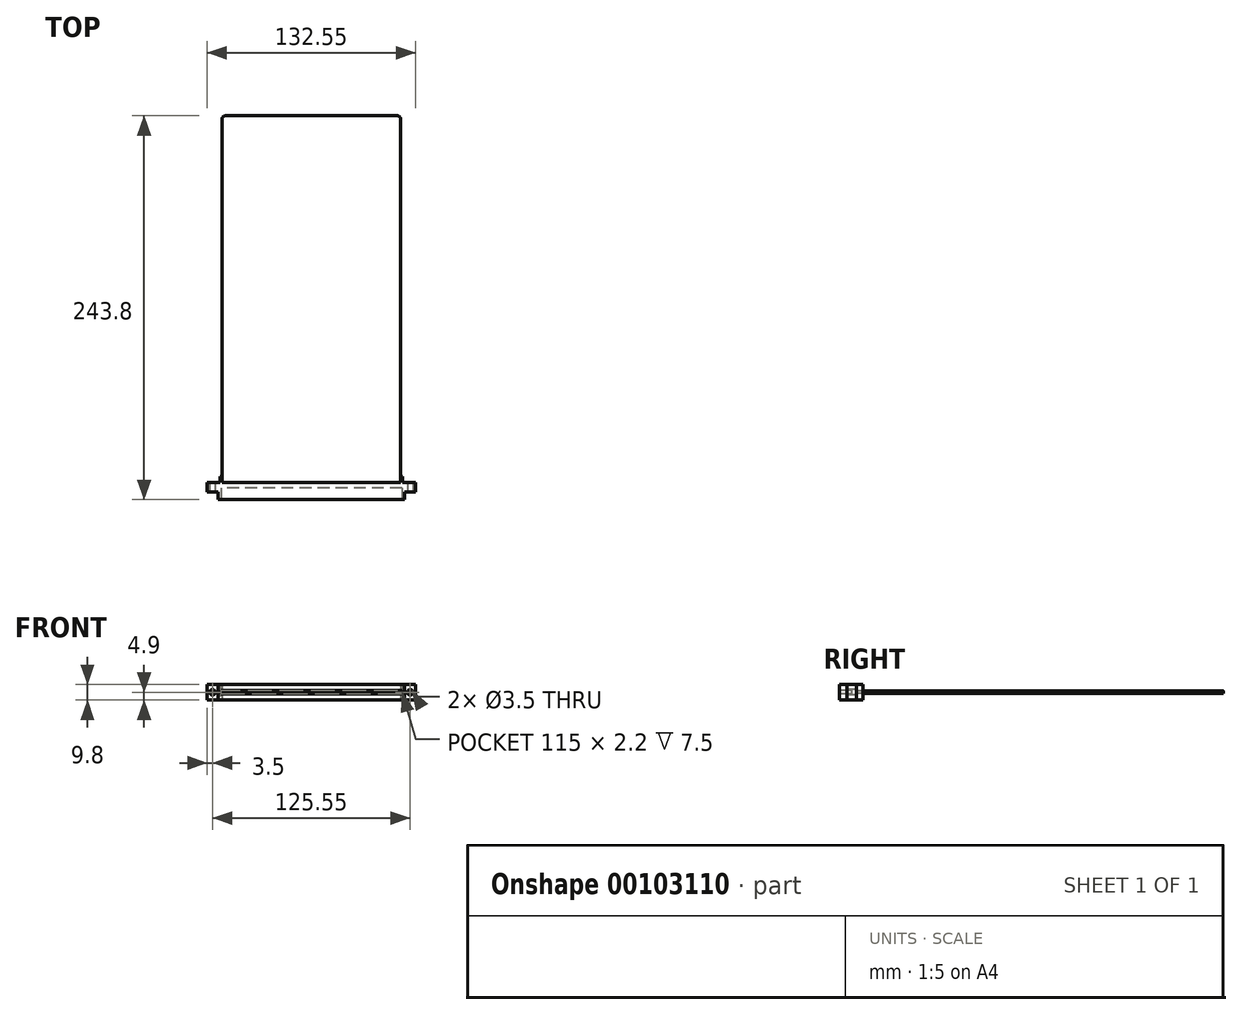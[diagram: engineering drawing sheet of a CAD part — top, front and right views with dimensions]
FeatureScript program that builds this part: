
annotation { "Feature Type Name" : "Feature", "Feature Type Description" : "" }
export const myFeature = defineFeature(function(context is Context, id is Id, definition is map)
    precondition{}
    {
        {
            var Q0;
            Q0=qCreatedBy(makeId("Top.planeOp"),FACE);
            var sketch = newSketch(context, id + "F0", { "sketchPlane" : qUnion([Q0])});
            skLineSegment(sketch, "E0.bottom", {"start": v(0, 6) * mm, "end": v(8.22, 6) * mm});
            skLineSegment(sketch, "E0.top", {"start": v(7, -4.8) * mm, "end": v(125.55, -4.8) * mm});
            skLineSegment(sketch, "E0.left", {"start": v(0, 6) * mm, "end": v(0, 0) * mm});
            skLineSegment(sketch, "E0.right", {"start": v(132.55, 6) * mm, "end": v(132.55, 0) * mm});
            skLineSegment(sketch, "E1.top", {"start": v(0, 0) * mm, "end": v(7, 0) * mm});
            skLineSegment(sketch, "E1.right", {"start": v(7, -4.8) * mm, "end": v(7, 0) * mm});
            skLineSegment(sketch, "E2.top", {"start": v(132.55, 0) * mm, "end": v(125.55, 0) * mm});
            skLineSegment(sketch, "E2.right", {"start": v(125.55, -4.8) * mm, "end": v(125.55, 0) * mm});
            skLineSegment(sketch, "E3.top", {"start": v(8.22, 10) * mm, "end": v(9.57, 10) * mm});
            skLineSegment(sketch, "E3.left", {"start": v(8.22, 6) * mm, "end": v(8.22, 10) * mm});
            skLineSegment(sketch, "E3.right", {"start": v(9.57, 6) * mm, "end": v(9.57, 10) * mm});
            skLineSegment(sketch, "E4.top", {"start": v(124.33, 10) * mm, "end": v(122.98, 10) * mm});
            skLineSegment(sketch, "E4.left", {"start": v(124.33, 6) * mm, "end": v(124.33, 10) * mm});
            skLineSegment(sketch, "E4.right", {"start": v(122.98, 6) * mm, "end": v(122.98, 10) * mm});
            skLineSegment(sketch, "E5.trimOffspring", {"start": v(124.33, 6) * mm, "end": v(132.55, 6) * mm});
            skLineSegment(sketch, "E6.trimOffspring", {"start": v(9.57, 6) * mm, "end": v(122.98, 6) * mm});
            skSolve(sketch);
        }
        {
            var Q0;
            Q0=makeQuery(id+"F0.imprint","IMPRINT",FACE,{"disambiguationData":[TD([[makeQuery(id+"F0.imprint","IMPRINT",EDGE,{"derivedFrom":sQuery(id+"F0.wireOp",EDGE,"E0.bottom")}),-1.0]])]});
            extrude(context, id + "F1", {"entities" : qUnion([Q0]), "depth" : 9.8 * mm});
        }
        {
            var Q0;
            Q0=makeQuery(id+"F1.opExtrude","SWEPT_FACE",FACE,{"disambiguationData":[OSD([sQuery(id+"F0.wireOp",EDGE,"E1.top")])]});
            var sketch = newSketch(context, id + "F2", { "sketchPlane" : qUnion([Q0])});
            skCircle(sketch, "E7", {"center": v(3.5, 4.9) * mm, "radius": 1.75 * mm});
            skPoint(sketch, "E7.centerSnap0", {"position": v(7, 4.9) * mm});
            skPoint(sketch, "E7.centerSnap1", {"position": v(3.5, 9.8) * mm});
            skSolve(sketch);
        }
        {
            var Q0;
            Q0=makeQuery(id+"F2.imprint","IMPRINT",FACE,{"disambiguationData":[TD([[makeQuery(id+"F2.imprint","IMPRINT",EDGE,{"derivedFrom":sQuery(id+"F2.wireOp",EDGE,"E7")}),1.0]])]});
            extrude(context, id + "F3", {"entities" : qUnion([Q0]), "operationType" : NewBodyOperationType.REMOVE, "oppositeDirection" : true, "depth" : 7 * mm});
        }
        {
            var Q0;
            Q0=makeQuery(id+"F1.opExtrude","SWEPT_FACE",FACE,{"disambiguationData":[OSD([sQuery(id+"F0.wireOp",EDGE,"E2.top")])]});
            var sketch = newSketch(context, id + "F4", { "sketchPlane" : qUnion([Q0])});
            skCircle(sketch, "E8", {"center": v(129.05, 4.9) * mm, "radius": 1.75 * mm});
            skPoint(sketch, "E8.centerSnap0", {"position": v(125.55, 4.9) * mm});
            skPoint(sketch, "E8.centerSnap1", {"position": v(129.05, 9.8) * mm});
            skSolve(sketch);
        }
        {
            var Q0;
            Q0 = qSketchRegion(id + "F4", true);
            var Q1;
            Q1=makeQuery(id+"F4.imprint","IMPRINT",FACE,{"disambiguationData":[TD([[makeQuery(id+"F4.imprint","IMPRINT",EDGE,{"derivedFrom":sQuery(id+"F4.wireOp",EDGE,"E8")}),1.0]])]});
            extrude(context, id + "F5", {"entities" : qUnion([Q0, Q1]), "operationType" : NewBodyOperationType.REMOVE, "oppositeDirection" : true, "depth" : 7 * mm});
        }
        {
            var Q0;
            Q0=makeQuery(id+"F1.opExtrude","SWEPT_FACE",FACE,{"disambiguationData":[OSD([sQuery(id+"F0.wireOp",EDGE,"E0.top")])]});
            var sketch = newSketch(context, id + "F6", { "sketchPlane" : qUnion([Q0])});
            skLineSegment(sketch, "E9.bottom", {"start": v(123.78, 6) * mm, "end": v(8.78, 6) * mm});
            skLineSegment(sketch, "E9.top", {"start": v(123.78, 3.8) * mm, "end": v(8.78, 3.8) * mm});
            skLineSegment(sketch, "E9.left", {"start": v(123.78, 6) * mm, "end": v(123.78, 3.8) * mm});
            skLineSegment(sketch, "E9.right", {"start": v(8.78, 6) * mm, "end": v(8.78, 3.8) * mm});
            skPoint(sketch, "E9.middle", {"position": v(66.28, 4.9) * mm});
            skPoint(sketch, "E9.middle.positionSnap0", {"position": v(7, 4.9) * mm});
            skPoint(sketch, "E9.middle.positionSnap1", {"position": v(66.28, 9.8) * mm});
            skPoint(sketch, "E9.centerSnap0", {"position": v(7, 4.9) * mm});
            skPoint(sketch, "E9.centerSnap1", {"position": v(66.28, 9.8) * mm});
            skSolve(sketch);
        }
        {
            var Q0;
            Q0=makeQuery(id+"F6.imprint","IMPRINT",FACE,{"disambiguationData":[TD([[makeQuery(id+"F6.imprint","IMPRINT",EDGE,{"derivedFrom":sQuery(id+"F6.wireOp",EDGE,"E9.bottom")}),1.0]])]});
            extrude(context, id + "F7", {"entities" : qUnion([Q0]), "operationType" : NewBodyOperationType.REMOVE, "oppositeDirection" : true, "depth" : 7.5 * mm});
        }
        {
            var Q0;
            Q0=makeQuery(id+"F1.opExtrude","SWEPT_FACE",FACE,{"disambiguationData":[OSD([sQuery(id+"F0.wireOp",EDGE,"E6.trimOffspring")])]});
            var sketch = newSketch(context, id + "F8", { "sketchPlane" : qUnion([Q0])});
            skLineSegment(sketch, "E10.bottom", {"start": v(-9.27, 4.1) * mm, "end": v(-123.27, 4.1) * mm});
            skLineSegment(sketch, "E10.top", {"start": v(-9.27, 5.7) * mm, "end": v(-123.27, 5.7) * mm});
            skLineSegment(sketch, "E10.left", {"start": v(-9.27, 4.1) * mm, "end": v(-9.27, 5.7) * mm});
            skLineSegment(sketch, "E10.right", {"start": v(-123.27, 4.1) * mm, "end": v(-123.27, 5.7) * mm});
            skPoint(sketch, "E10.middle", {"position": v(-66.28, 4.9) * mm});
            skPoint(sketch, "E10.middle.positionSnap0", {"position": v(-66.28, 9.8) * mm});
            skPoint(sketch, "E10.middle.positionSnap1", {"position": v(-122.98, 4.9) * mm});
            skPoint(sketch, "E10.centerSnap0", {"position": v(-66.28, 9.8) * mm});
            skPoint(sketch, "E10.centerSnap1", {"position": v(-122.98, 4.9) * mm});
            skSolve(sketch);
        }
        {
            var Q0;
            {var subQ0=sQuery(id+"F8.wireOp",EDGE,"E10.bottom");var subQ1=sQuery(id+"F0.wireOp",EDGE,"E6.trimOffspring");var subQ2=makeQuery(id+"F1.opExtrude","SWEPT_EDGE",EDGE,{"disambiguationData":[OSD([sQuery(id+"F0.wireOp",EDGE,"E3.right"),subQ1])]});var subQ3=makeQuery(id+"F8.imprint","INTERSECT",VERTEX,{"derivedFrom":[subQ2,subQ0]});Q0=makeQuery(id+"F8.imprint","IMPRINT",FACE,{"disambiguationData":[TD([[makeQuery(id+"F8.imprint","IMPRINT",EDGE,{"disambiguationData":[TD([[subQ3,-1.0]])],"derivedFrom":subQ0}),-1.0]])]});}
            extrude(context, id + "F9", {"entities" : qUnion([Q0]), "operationType" : NewBodyOperationType.ADD, "depth" : 233 * mm});
        }
        {
            var Q0;
            Q0=makeQuery(id+"F9.opExtrude","CAP_EDGE",EDGE,{"disambiguationData":[OSD([sQuery(id+"F0.wireOp",EDGE,"E4.right"),sQuery(id+"F0.wireOp",EDGE,"E6.trimOffspring")])],"isStart":false});
            var Q1;
            Q1=makeQuery(id+"F9.opExtrude","CAP_EDGE",EDGE,{"disambiguationData":[OSD([sQuery(id+"F0.wireOp",EDGE,"E3.right"),sQuery(id+"F0.wireOp",EDGE,"E6.trimOffspring")])],"isStart":false});
            fillet(context, id + "F10", {"entities" : qUnion([Q0, Q1]), "radius" : 2 * mm, "tangentPropagation" : true, "allowEdgeOverflow" : false});
        }
    });
